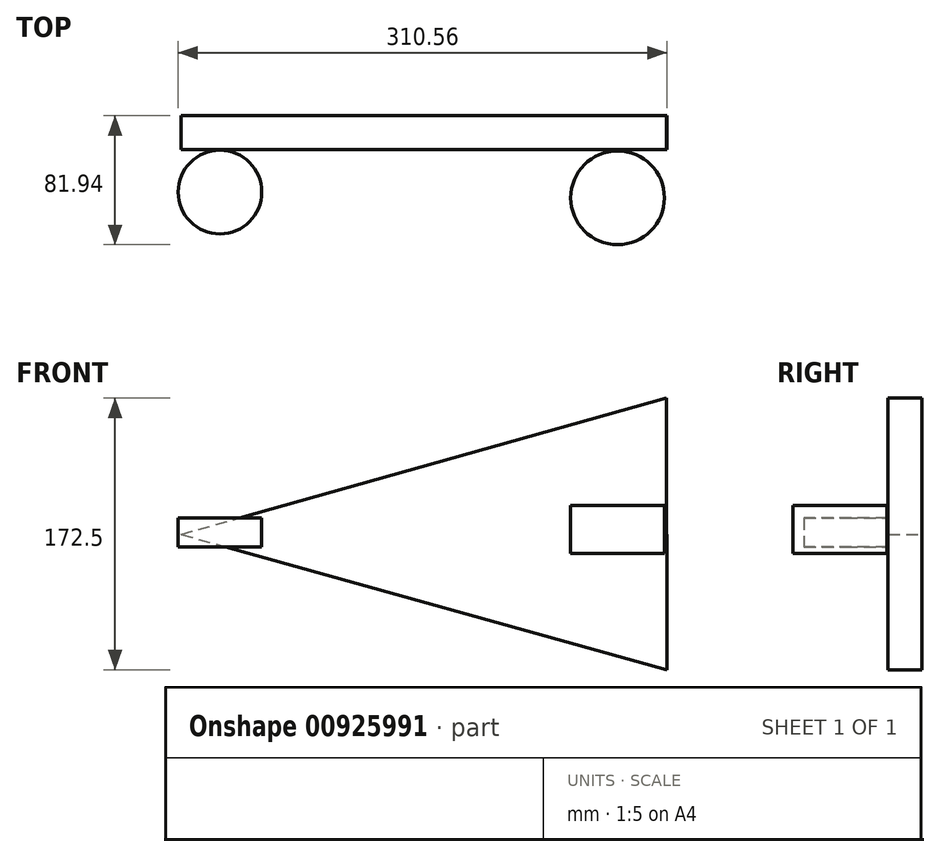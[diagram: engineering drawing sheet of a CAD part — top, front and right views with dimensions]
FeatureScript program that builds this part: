
annotation { "Feature Type Name" : "Feature", "Feature Type Description" : "" }
export const myFeature = defineFeature(function(context is Context, id is Id, definition is map)
    precondition{}
    {
        {
            var Q0;
            Q0=qCreatedBy(makeId("Front.planeOp"),FACE);
            var sketch = newSketch(context, id + "F0", { "sketchPlane" : qUnion([Q0])});
            skLineSegment(sketch, "E0", {"start": v(-154.43, 0) * mm, "end": v(154, 86.49) * mm});
            skLineSegment(sketch, "E1", {"start": v(-154.43, 0) * mm, "end": v(154.32, -86) * mm});
            skLineSegment(sketch, "E2", {"start": v(154, 86.49) * mm, "end": v(154.32, -86) * mm});
            skSolve(sketch);
        }
        {
            var Q0;
            Q0=makeQuery(id+"F0.imprint","IMPRINT",FACE,{"disambiguationData":[TD([[makeQuery(id+"F0.imprint","IMPRINT",EDGE,{"derivedFrom":sQuery(id+"F0.wireOp",EDGE,"E0")}),-1.0]])]});
            extrude(context, id + "F1", {"entities" : qUnion([Q0]), "depth" : 21.59 * mm, "offsetDistance" : 25.4 * mm});
        }
        {
            var Q0;
            Q0=qCreatedBy(makeId("Top.planeOp"),FACE);
            var sketch = newSketch(context, id + "F2", { "sketchPlane" : qUnion([Q0])});
            skCircle(sketch, "E3", {"center": v(-129.69, -48.48) * mm, "radius": 26.56 * mm});
            skSolve(sketch);
        }
        {
            var Q0;
            Q0=makeQuery(id+"F2.imprint","IMPRINT",FACE,{"disambiguationData":[TD([[makeQuery(id+"F2.imprint","IMPRINT",EDGE,{"derivedFrom":sQuery(id+"F2.wireOp",EDGE,"E3")}),1.0]])]});
            var Q1;
            Q1=sQuery(id+"F2.wireOp",EDGE,"E3");
            extrude(context, id + "F3", {"entities" : qUnion([Q0]), "surfaceEntities" : qUnion([Q1]), "depth" : 10.4 * mm, "offsetDistance" : 25.4 * mm, "hasSecondDirection" : true, "secondDirectionOppositeDirection" : true, "secondDirectionDepth" : 7.87 * mm});
        }
        {
            var Q0;
            Q0=makeQuery(id+"F3.opExtrude","CAP_FACE",FACE,{"disambiguationData":[OSD([sQuery(id+"F2.wireOp",EDGE,"E3")])],"isStart":false});
            var sketch = newSketch(context, id + "F4", { "sketchPlane" : qUnion([Q0])});
            skCircle(sketch, "E4", {"center": v(122.85, -52.16) * mm, "radius": 29.78 * mm});
            skSolve(sketch);
        }
        {
            var Q0;
            Q0=makeQuery(id+"F4.imprint","IMPRINT",FACE,{"disambiguationData":[TD([[makeQuery(id+"F4.imprint","IMPRINT",EDGE,{"derivedFrom":sQuery(id+"F4.wireOp",EDGE,"E4")}),1.0]])]});
            extrude(context, id + "F5", {"entities" : qUnion([Q0]), "depth" : 7.87 * mm, "offsetDistance" : 25.4 * mm, "hasSecondDirection" : true, "secondDirectionOppositeDirection" : true, "secondDirectionDepth" : 22.6 * mm});
        }
    });
